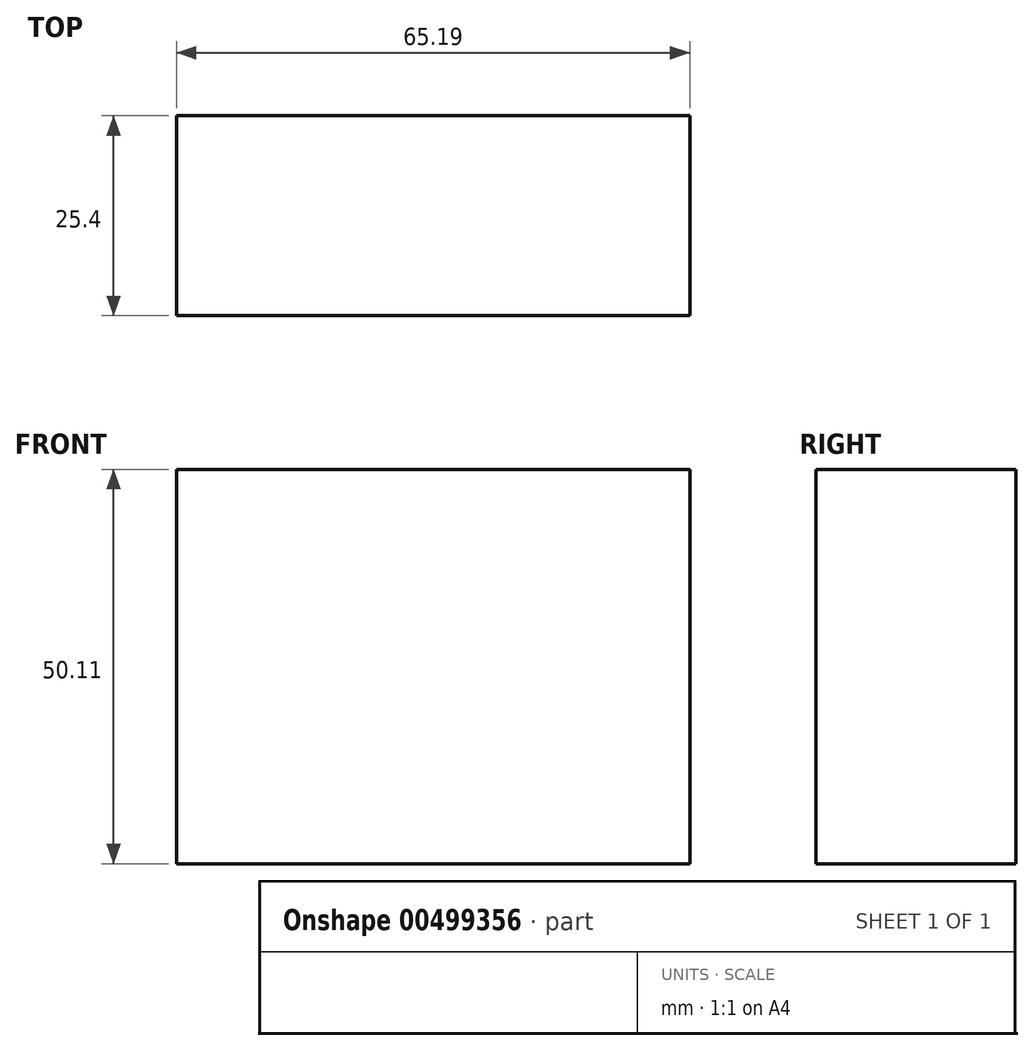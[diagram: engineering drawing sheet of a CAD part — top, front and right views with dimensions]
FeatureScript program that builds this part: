
annotation { "Feature Type Name" : "Feature", "Feature Type Description" : "" }
export const myFeature = defineFeature(function(context is Context, id is Id, definition is map)
    precondition{}
    {
        {
            var Q0;
            Q0=qCreatedBy(makeId("Front.planeOp"),FACE);
            var sketch = newSketch(context, id + "F0", { "sketchPlane" : qUnion([Q0])});
            skLineSegment(sketch, "E0.bottom", {"start": v(-57.38, 69.17) * mm, "end": v(7.8, 69.17) * mm});
            skLineSegment(sketch, "E0.top", {"start": v(-57.38, 19.06) * mm, "end": v(7.8, 19.06) * mm});
            skLineSegment(sketch, "E0.left", {"start": v(-57.38, 69.17) * mm, "end": v(-57.38, 19.06) * mm});
            skLineSegment(sketch, "E0.right", {"start": v(7.8, 69.17) * mm, "end": v(7.8, 19.06) * mm});
            skSolve(sketch);
        }
        {
            var Q0;
            Q0=makeQuery(id+"F0.imprint","IMPRINT",FACE,{"disambiguationData":[TD([[makeQuery(id+"F0.imprint","IMPRINT",EDGE,{"derivedFrom":sQuery(id+"F0.wireOp",EDGE,"E0.bottom")}),-1.0]])]});
            extrude(context, id + "F1", {"entities" : qUnion([Q0]), "depth" : 25.4 * mm});
        }
    });
